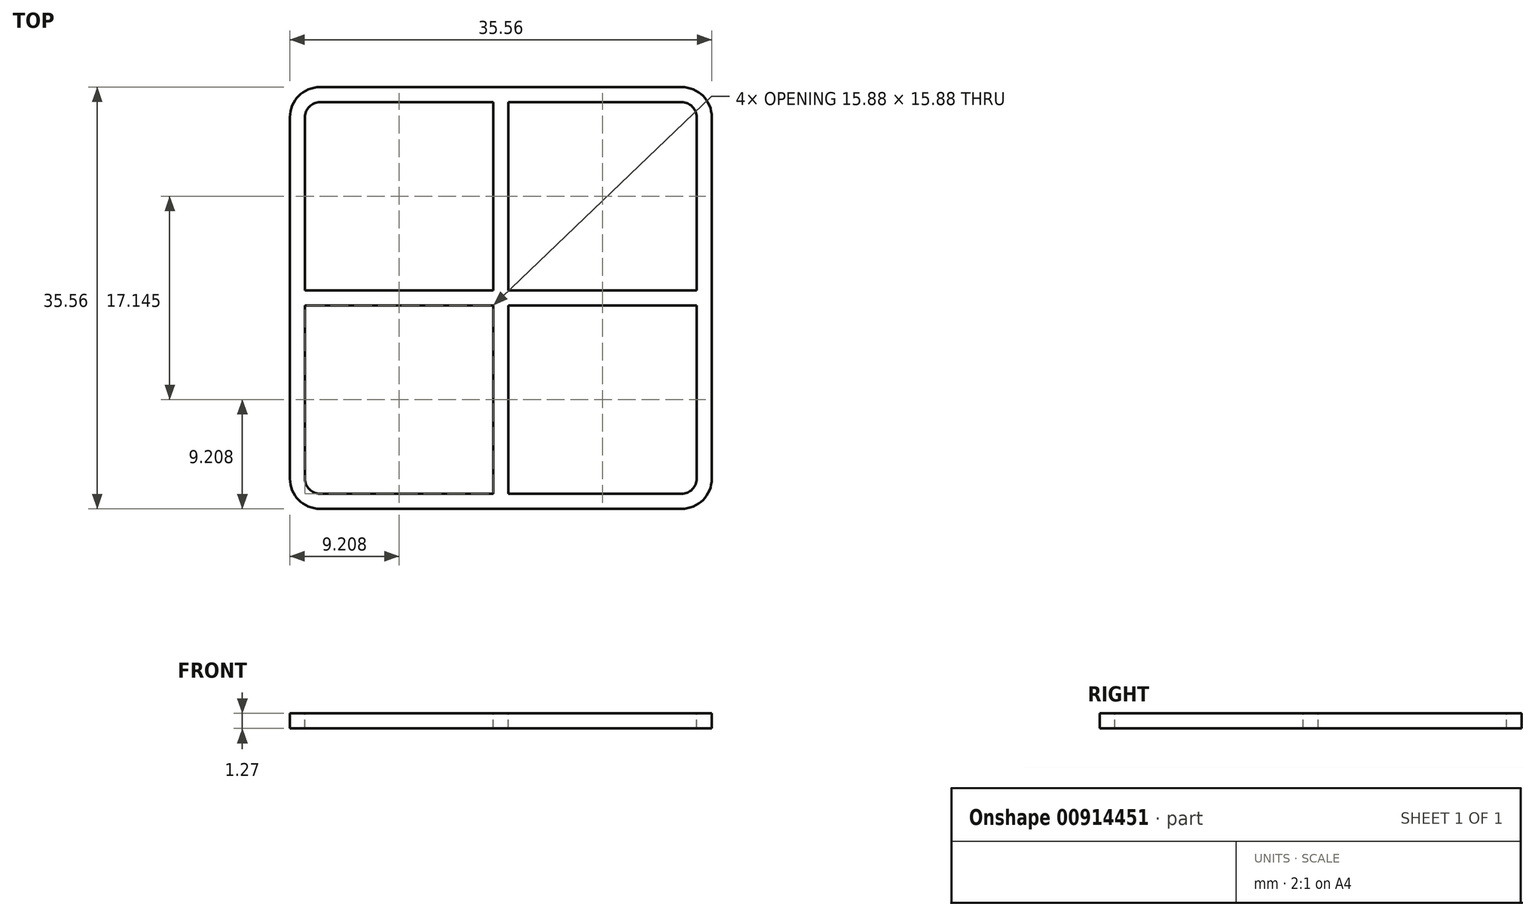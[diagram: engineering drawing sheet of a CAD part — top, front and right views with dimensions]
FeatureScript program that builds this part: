
annotation { "Feature Type Name" : "Feature", "Feature Type Description" : "" }
export const myFeature = defineFeature(function(context is Context, id is Id, definition is map)
    precondition{}
    {
        {
            var Q0;
            Q0=qCreatedBy(makeId("Top.planeOp"),FACE);
            var sketch = newSketch(context, id + "F0", { "sketchPlane" : qUnion([Q0])});
            skLineSegment(sketch, "E0.bottom", {"start": v(17.78, -17.78) * mm, "end": v(-17.78, -17.78) * mm});
            skLineSegment(sketch, "E0.top", {"start": v(17.78, 17.78) * mm, "end": v(-17.78, 17.78) * mm});
            skLineSegment(sketch, "E0.left", {"start": v(17.78, -17.78) * mm, "end": v(17.78, 17.78) * mm});
            skLineSegment(sketch, "E0.right", {"start": v(-17.78, -17.78) * mm, "end": v(-17.78, 17.78) * mm});
            skPoint(sketch, "E0.middle", {"position": v(0, 0) * mm});
            skLineSegment(sketch, "E1.bottom", {"start": v(-16.51, -16.5) * mm, "end": v(-0.64, -16.51) * mm});
            skLineSegment(sketch, "E1.top", {"start": v(-16.51, -0.64) * mm, "end": v(-0.64, -0.63) * mm});
            skLineSegment(sketch, "E1.left", {"start": v(-16.51, -16.5) * mm, "end": v(-16.51, -0.63) * mm});
            skLineSegment(sketch, "E1.right", {"start": v(-0.64, -16.51) * mm, "end": v(-0.63, -0.64) * mm});
            skLineSegment(sketch, "E2.1.0", {"start": v(16.51, -16.51) * mm, "end": v(16.51, -0.64) * mm});
            skLineSegment(sketch, "E2.1.1", {"start": v(16.51, -0.63) * mm, "end": v(0.64, -0.63) * mm});
            skLineSegment(sketch, "E2.1.3", {"start": v(16.5, -16.51) * mm, "end": v(0.63, -16.51) * mm});
            skLineSegment(sketch, "E2.1.4", {"start": v(0.64, -16.51) * mm, "end": v(0.63, -0.63) * mm});
            skLineSegment(sketch, "E2.2.0", {"start": v(16.51, 16.51) * mm, "end": v(0.64, 16.51) * mm});
            skLineSegment(sketch, "E2.2.1", {"start": v(0.63, 16.51) * mm, "end": v(0.63, 0.64) * mm});
            skLineSegment(sketch, "E2.2.3", {"start": v(16.51, 16.5) * mm, "end": v(16.51, 0.63) * mm});
            skLineSegment(sketch, "E2.2.4", {"start": v(16.51, 0.64) * mm, "end": v(0.63, 0.63) * mm});
            skLineSegment(sketch, "E2.3.0", {"start": v(-16.51, 16.51) * mm, "end": v(-16.51, 0.64) * mm});
            skLineSegment(sketch, "E2.3.1", {"start": v(-16.51, 0.63) * mm, "end": v(-0.64, 0.63) * mm});
            skLineSegment(sketch, "E2.3.3", {"start": v(-16.5, 16.51) * mm, "end": v(-0.64, 16.51) * mm});
            skLineSegment(sketch, "E2.3.4", {"start": v(-0.64, 16.51) * mm, "end": v(-0.63, 0.63) * mm});
            skSolve(sketch);
        }
        {
            var Q0;
            Q0=makeQuery(id+"F0.imprint","IMPRINT",FACE,{"disambiguationData":[TD([[makeQuery(id+"F0.imprint","IMPRINT",EDGE,{"derivedFrom":sQuery(id+"F0.wireOp",EDGE,"E0.bottom")}),-1.0]])]});
            extrude(context, id + "F1", {"entities" : qUnion([Q0]), "oppositeDirection" : true, "depth" : 1.27 * mm, "offsetDistance" : 25.4 * mm});
        }
        {
            var Q0;
            Q0=makeQuery(id+"F1.opExtrude","SWEPT_EDGE",EDGE,{"disambiguationData":[OSD([sQuery(id+"F0.wireOp",EDGE,"E0.bottom"),sQuery(id+"F0.wireOp",EDGE,"E0.right")])]});
            var Q1;
            Q1=makeQuery(id+"F1.opExtrude","SWEPT_EDGE",EDGE,{"disambiguationData":[OSD([sQuery(id+"F0.wireOp",EDGE,"E0.bottom"),sQuery(id+"F0.wireOp",EDGE,"E0.left")])]});
            var Q2;
            Q2=makeQuery(id+"F1.opExtrude","SWEPT_EDGE",EDGE,{"disambiguationData":[OSD([sQuery(id+"F0.wireOp",EDGE,"E0.top"),sQuery(id+"F0.wireOp",EDGE,"E0.left")])]});
            var Q3;
            Q3=makeQuery(id+"F1.opExtrude","SWEPT_EDGE",EDGE,{"disambiguationData":[OSD([sQuery(id+"F0.wireOp",EDGE,"E0.top"),sQuery(id+"F0.wireOp",EDGE,"E0.right")])]});
            fillet(context, id + "F2", {"entities" : qUnion([Q0, Q1, Q2, Q3]), "radius" : 2.54 * mm, "tangentPropagation" : true, "allowEdgeOverflow" : false});
        }
        {
            var Q0;
            Q0=makeQuery(id+"F1.opExtrude","SWEPT_EDGE",EDGE,{"disambiguationData":[OSD([sQuery(id+"F0.wireOp",EDGE,"E2.3.0"),sQuery(id+"F0.wireOp",EDGE,"E2.3.3")])]});
            var Q1;
            Q1=makeQuery(id+"F1.opExtrude","SWEPT_EDGE",EDGE,{"disambiguationData":[OSD([sQuery(id+"F0.wireOp",EDGE,"E2.2.0"),sQuery(id+"F0.wireOp",EDGE,"E2.2.3")])]});
            var Q2;
            Q2=makeQuery(id+"F1.opExtrude","SWEPT_EDGE",EDGE,{"disambiguationData":[OSD([sQuery(id+"F0.wireOp",EDGE,"E2.1.0"),sQuery(id+"F0.wireOp",EDGE,"E2.1.3")])]});
            var Q3;
            Q3=makeQuery(id+"F1.opExtrude","SWEPT_EDGE",EDGE,{"disambiguationData":[OSD([sQuery(id+"F0.wireOp",EDGE,"E1.bottom"),sQuery(id+"F0.wireOp",EDGE,"E1.left")])]});
            fillet(context, id + "F3", {"entities" : qUnion([Q0, Q1, Q2, Q3]), "radius" : 1.27 * mm, "tangentPropagation" : true, "allowEdgeOverflow" : false});
        }
    });
